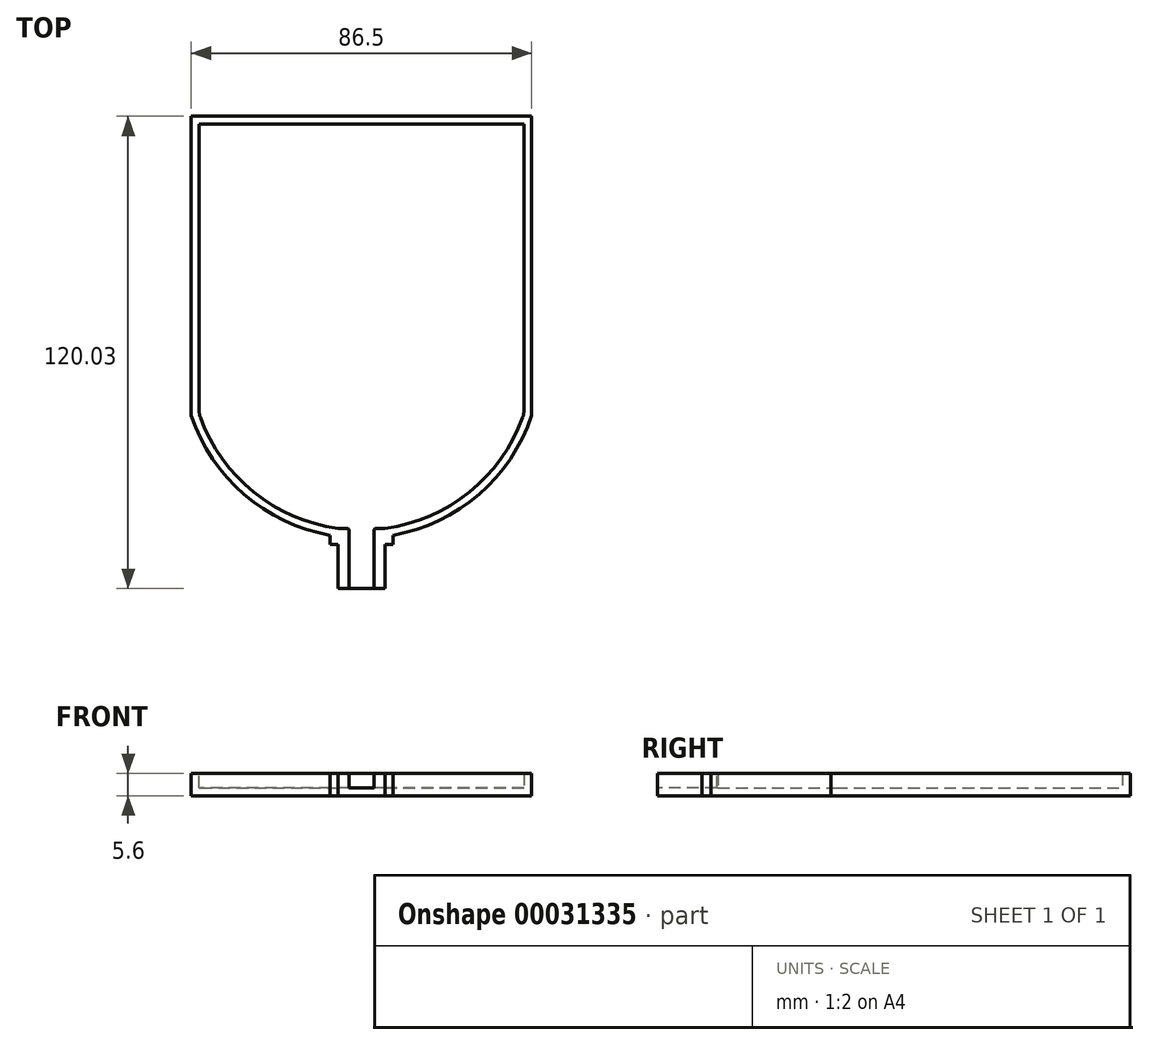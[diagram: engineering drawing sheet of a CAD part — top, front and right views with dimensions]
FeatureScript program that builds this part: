
annotation { "Feature Type Name" : "Feature", "Feature Type Description" : "" }
export const myFeature = defineFeature(function(context is Context, id is Id, definition is map)
    precondition{}
    {
        {
            var Q0;
            Q0=qCreatedBy(makeId("Top.planeOp"),FACE);
            var sketch = newSketch(context, id + "F0", { "sketchPlane" : qUnion([Q0])});
            skLineSegment(sketch, "E0.bottom", {"start": v(-41.08, 29.97) * mm, "end": v(45.42, 29.97) * mm});
            skLineSegment(sketch, "E0.top", {"start": v(-41.08, -46.03) * mm, "end": v(45.42, -46.03) * mm});
            skLineSegment(sketch, "E0.left", {"start": v(-41.08, 29.97) * mm, "end": v(-41.08, -46.03) * mm});
            skLineSegment(sketch, "E0.right", {"start": v(45.42, 29.97) * mm, "end": v(45.42, -46.03) * mm});
            skArc(sketch, "E1", {"start": v(-41.08, -46.03) * mm, "mid": v(2.17, -77.2) * mm, "end": v(45.42, -46.03) * mm});
            skLineSegment(sketch, "E2", {"start": v(2.17, -46.03) * mm, "end": v(2.17, -77.2) * mm});
            skLineSegment(sketch, "E3.bottom", {"start": v(2.17, -77.2) * mm, "end": v(8.1, -77.2) * mm});
            skLineSegment(sketch, "E3.top", {"start": v(2.17, -90.06) * mm, "end": v(8.1, -90.06) * mm});
            skLineSegment(sketch, "E3.left", {"start": v(2.17, -77.2) * mm, "end": v(2.17, -90.06) * mm});
            skLineSegment(sketch, "E3.right", {"start": v(8.1, -77.2) * mm, "end": v(8.1, -90.06) * mm});
            skLineSegment(sketch, "E4.bottom", {"start": v(2.17, -77.2) * mm, "end": v(-3.75, -77.2) * mm});
            skLineSegment(sketch, "E4.top", {"start": v(2.17, -90.06) * mm, "end": v(-3.75, -90.06) * mm});
            skLineSegment(sketch, "E4.right", {"start": v(-3.75, -77.2) * mm, "end": v(-3.75, -90.06) * mm});
            skLineSegment(sketch, "E5.bottom", {"start": v(-5.83, -76.5) * mm, "end": v(2.17, -76.5) * mm});
            skLineSegment(sketch, "E5.top", {"start": v(-5.83, -78.8) * mm, "end": v(2.17, -78.8) * mm});
            skLineSegment(sketch, "E5.left", {"start": v(-5.83, -76.5) * mm, "end": v(-5.83, -78.8) * mm});
            skLineSegment(sketch, "E5.right", {"start": v(2.17, -76.5) * mm, "end": v(2.17, -78.8) * mm});
            skLineSegment(sketch, "E6.bottom", {"start": v(2.17, -78.8) * mm, "end": v(10.17, -78.8) * mm});
            skLineSegment(sketch, "E6.top", {"start": v(2.17, -76.5) * mm, "end": v(10.17, -76.5) * mm});
            skLineSegment(sketch, "E6.left", {"start": v(2.17, -78.8) * mm, "end": v(2.17, -76.5) * mm});
            skLineSegment(sketch, "E6.right", {"start": v(10.17, -78.8) * mm, "end": v(10.17, -76.5) * mm});
            skLineSegment(sketch, "E7.0", {"start": v(-39.08, 27.97) * mm, "end": v(43.42, 27.97) * mm});
            skLineSegment(sketch, "E7.1", {"start": v(-39.08, 27.97) * mm, "end": v(-39.08, -45.7) * mm});
            skArc(sketch, "E7.2", {"start": v(-39.08, -45.7) * mm, "mid": v(2.17, -75.2) * mm, "end": v(43.42, -45.7) * mm});
            skLineSegment(sketch, "E7.3", {"start": v(43.42, 27.97) * mm, "end": v(43.42, -45.7) * mm});
            skSolve(sketch);
        }
        {
            var Q0;
            {var subQ1=sQuery(id+"F0.wireOp",EDGE,"E2");var subQ3=sQuery(id+"F0.wireOp",EDGE,"E0.top");var subQ5=makeQuery(id+"F0.imprint","INTERSECT",VERTEX,{"derivedFrom":[subQ3,subQ1]});Q0=makeQuery(id+"F0.imprint","IMPRINT",FACE,{"disambiguationData":[TD([[makeQuery(id+"F0.imprint","IMPRINT",EDGE,{"disambiguationData":[TD([[subQ5,-1.0]])],"derivedFrom":subQ3}),-1.0]])]});}
            var Q1;
            {var subQ1=sQuery(id+"F0.wireOp",EDGE,"E2");var subQ3=sQuery(id+"F0.wireOp",EDGE,"E0.top");var subQ5=makeQuery(id+"F0.imprint","INTERSECT",VERTEX,{"derivedFrom":[subQ3,subQ1]});Q1=makeQuery(id+"F0.imprint","IMPRINT",FACE,{"disambiguationData":[TD([[makeQuery(id+"F0.imprint","IMPRINT",EDGE,{"disambiguationData":[TD([[subQ5,1.0]])],"derivedFrom":subQ3}),-1.0]])]});}
            var Q2;
            Q2=makeQuery(id+"F0.imprint","IMPRINT",FACE,{"disambiguationData":[TD([[makeQuery(id+"F0.imprint","IMPRINT",EDGE,{"derivedFrom":sQuery(id+"F0.wireOp",EDGE,"E0.bottom")}),-1.0]])]});
            var Q3;
            {var subQ5=sQuery(id+"F0.wireOp",EDGE,"E5.bottom");Q3=makeQuery(id+"F0.imprint","IMPRINT",FACE,{"disambiguationData":[TD([[makeQuery(id+"F0.imprint","IMPRINT",EDGE,{"derivedFrom":subQ5}),1.0]])]});}
            var Q4;
            {var subQ5=sQuery(id+"F0.wireOp",EDGE,"E6.top");Q4=makeQuery(id+"F0.imprint","IMPRINT",FACE,{"disambiguationData":[TD([[makeQuery(id+"F0.imprint","IMPRINT",EDGE,{"derivedFrom":subQ5}),1.0]])]});}
            var Q5;
            Q5=makeQuery(id+"F0.imprint","IMPRINT",FACE,{"disambiguationData":[TD([[makeQuery(id+"F0.imprint","IMPRINT",EDGE,{"derivedFrom":sQuery(id+"F0.wireOp",EDGE,"E7.0")}),-1.0]])]});
            var Q6;
            {var subQ4=sQuery(id+"F0.wireOp",EDGE,"E3.top");Q6=makeQuery(id+"F0.imprint","IMPRINT",FACE,{"disambiguationData":[TD([[makeQuery(id+"F0.imprint","IMPRINT",EDGE,{"derivedFrom":subQ4}),1.0]])]});}
            var Q7;
            {var subQ4=sQuery(id+"F0.wireOp",EDGE,"E4.top");Q7=makeQuery(id+"F0.imprint","IMPRINT",FACE,{"disambiguationData":[TD([[makeQuery(id+"F0.imprint","IMPRINT",EDGE,{"derivedFrom":subQ4}),-1.0]])]});}
            var Q8;
            {var subQ3=sQuery(id+"F0.wireOp",EDGE,"E4.bottom");Q8=makeQuery(id+"F0.imprint","IMPRINT",FACE,{"disambiguationData":[TD([[makeQuery(id+"F0.imprint","IMPRINT",EDGE,{"derivedFrom":subQ3}),1.0]])]});}
            var Q9;
            {var subQ4=sQuery(id+"F0.wireOp",EDGE,"E4.bottom");Q9=makeQuery(id+"F0.imprint","IMPRINT",FACE,{"disambiguationData":[TD([[makeQuery(id+"F0.imprint","IMPRINT",EDGE,{"derivedFrom":subQ4}),-1.0]])]});}
            var Q10;
            {var subQ4=sQuery(id+"F0.wireOp",EDGE,"E3.bottom");Q10=makeQuery(id+"F0.imprint","IMPRINT",FACE,{"disambiguationData":[TD([[makeQuery(id+"F0.imprint","IMPRINT",EDGE,{"derivedFrom":subQ4}),1.0]])]});}
            var Q11;
            {var subQ3=sQuery(id+"F0.wireOp",EDGE,"E3.bottom");Q11=makeQuery(id+"F0.imprint","IMPRINT",FACE,{"disambiguationData":[TD([[makeQuery(id+"F0.imprint","IMPRINT",EDGE,{"derivedFrom":subQ3}),-1.0]])]});}
            var Q12;
            {var subQ3=sQuery(id+"F0.wireOp",EDGE,"E5.bottom");Q12=makeQuery(id+"F0.imprint","IMPRINT",FACE,{"disambiguationData":[TD([[makeQuery(id+"F0.imprint","IMPRINT",EDGE,{"derivedFrom":subQ3}),-1.0]])]});}
            var Q13;
            {var subQ3=sQuery(id+"F0.wireOp",EDGE,"E6.top");Q13=makeQuery(id+"F0.imprint","IMPRINT",FACE,{"disambiguationData":[TD([[makeQuery(id+"F0.imprint","IMPRINT",EDGE,{"derivedFrom":subQ3}),-1.0]])]});}
            var Q14;
            Q14=sQuery(id+"F0.wireOp",EDGE,"E0.bottom");
            var Q15;
            Q15=sQuery(id+"F0.wireOp",EDGE,"E0.right");
            var Q16;
            Q16=sQuery(id+"F0.wireOp",EDGE,"E1");
            var Q17;
            Q17=sQuery(id+"F0.wireOp",EDGE,"E0.left");
            extrude(context, id + "F1", {"entities" : qUnion([Q0, Q1, Q2, Q3, Q4, Q5, Q6, Q7, Q8, Q9, Q10, Q11, Q12, Q13]), "surfaceEntities" : qUnion([Q14, Q15, Q16, Q17]), "endBound" : BoundingType.SYMMETRIC, "depth" : 2 * mm});
        }
        {
            var Q0;
            Q0=makeQuery(id+"F1.opExtrude","CAP_FACE",FACE,{"disambiguationData":[OSD([sQuery(id+"F0.wireOp",EDGE,"E0.bottom"),sQuery(id+"F0.wireOp",EDGE,"E0.left"),sQuery(id+"F0.wireOp",EDGE,"E0.right"),sQuery(id+"F0.wireOp",EDGE,"E1"),sQuery(id+"F0.wireOp",EDGE,"E3.top"),sQuery(id+"F0.wireOp",EDGE,"E3.right"),sQuery(id+"F0.wireOp",EDGE,"E4.top"),sQuery(id+"F0.wireOp",EDGE,"E4.right"),sQuery(id+"F0.wireOp",EDGE,"E5.top"),sQuery(id+"F0.wireOp",EDGE,"E5.left"),sQuery(id+"F0.wireOp",EDGE,"E6.bottom"),sQuery(id+"F0.wireOp",EDGE,"E6.right")])],"isStart":false});
            var sketch = newSketch(context, id + "F2", { "sketchPlane" : qUnion([Q0])});
            skLineSegment(sketch, "E8.0", {"start": v(43.42, 27.97) * mm, "end": v(-39.08, 27.97) * mm});
            skLineSegment(sketch, "E8.1", {"start": v(43.42, -45.7) * mm, "end": v(43.42, 27.97) * mm});
            skArc(sketch, "E8.2", {"start": v(8.17, -74.8) * mm, "mid": v(29.92, -65.24) * mm, "end": v(43.42, -45.7) * mm});
            skLineSegment(sketch, "E8.3", {"start": v(8.17, -76.8) * mm, "end": v(8.17, -74.8) * mm});
            skLineSegment(sketch, "E8.4", {"start": v(6.1, -76.8) * mm, "end": v(8.17, -76.8) * mm});
            skLineSegment(sketch, "E8.5", {"start": v(-39.08, 27.97) * mm, "end": v(-39.08, -45.7) * mm});
            skLineSegment(sketch, "E8.6", {"start": v(6.1, -88.06) * mm, "end": v(6.1, -76.8) * mm});
            skLineSegment(sketch, "E8.7", {"start": v(-1.75, -88.06) * mm, "end": v(6.1, -88.06) * mm});
            skLineSegment(sketch, "E8.8", {"start": v(-1.75, -76.8) * mm, "end": v(-1.75, -88.06) * mm});
            skLineSegment(sketch, "E8.9", {"start": v(-3.83, -76.8) * mm, "end": v(-1.75, -76.8) * mm});
            skLineSegment(sketch, "E8.10", {"start": v(-3.83, -74.8) * mm, "end": v(-3.83, -76.8) * mm});
            skArc(sketch, "E8.11", {"start": v(-39.08, -45.7) * mm, "mid": v(-25.57, -65.24) * mm, "end": v(-3.83, -74.8) * mm});
            skLineSegment(sketch, "E9", {"start": v(2.17, -88.06) * mm, "end": v(2.17, -74.8) * mm});
            skLineSegment(sketch, "E10", {"start": v(2.17, -74.8) * mm, "end": v(5.32, -74.8) * mm});
            skLineSegment(sketch, "E11", {"start": v(5.32, -74.8) * mm, "end": v(2.17, -74.8) * mm});
            skLineSegment(sketch, "E12", {"start": v(2.17, -74.8) * mm, "end": v(-0.98, -74.8) * mm});
            skLineSegment(sketch, "E13", {"start": v(-0.98, -74.8) * mm, "end": v(-0.98, -90.06) * mm});
            skLineSegment(sketch, "E14", {"start": v(-0.98, -90.06) * mm, "end": v(5.32, -90.06) * mm});
            skLineSegment(sketch, "E15", {"start": v(5.32, -90.06) * mm, "end": v(5.32, -74.8) * mm});
            skLineSegment(sketch, "E16", {"start": v(8.17, -74.8) * mm, "end": v(5.32, -74.8) * mm});
            skLineSegment(sketch, "E17", {"start": v(-0.98, -74.8) * mm, "end": v(-3.83, -74.8) * mm});
            skSolve(sketch);
        }
        {
            var Q0;
            Q0=makeQuery(id+"F2.imprint","IMPRINT",FACE,{"disambiguationData":[TD([[makeQuery(id+"F2.imprint","IMPRINT",EDGE,{"derivedFrom":sQuery(id+"F2.wireOp",EDGE,"E8.0")}),-1.0]])]});
            var Q1;
            {var subQ4=sQuery(id+"F2.wireOp",EDGE,"E8.8");Q1=makeQuery(id+"F2.imprint","IMPRINT",FACE,{"disambiguationData":[TD([[makeQuery(id+"F2.imprint","IMPRINT",EDGE,{"derivedFrom":subQ4}),1.0]])]});}
            var Q2;
            Q2=makeQuery(id+"F2.imprint","IMPRINT",FACE,{"disambiguationData":[TD([[makeQuery(id+"F2.imprint","IMPRINT",EDGE,{"derivedFrom":sQuery(id+"F2.wireOp",EDGE,"E8.3")}),1.0]])]});
            extrude(context, id + "F3", {"entities" : qUnion([Q0, Q1, Q2]), "operationType" : NewBodyOperationType.ADD, "depth" : 3.6 * mm});
        }
        {
            var Q0;
            Q0=makeQuery(id+"F3.opExtrude","SWEPT_EDGE",EDGE,{"disambiguationData":[OSD([sQuery(id+"F2.wireOp",EDGE,"E8.5"),sQuery(id+"F2.wireOp",EDGE,"E8.11")])]});
            var Q1;
            Q1=makeQuery(id+"F3.opExtrude","SWEPT_EDGE",EDGE,{"disambiguationData":[OSD([sQuery(id+"F2.wireOp",EDGE,"E8.1"),sQuery(id+"F2.wireOp",EDGE,"E8.2")])]});
            fillet(context, id + "F4", {"entities" : qUnion([Q0, Q1]), "radius" : 5 * mm, "tangentPropagation" : true, "allowEdgeOverflow" : false});
        }
        {
            var Q0;
            Q0=makeQuery(id+"F3.opExtrude","SWEPT_EDGE",EDGE,{"disambiguationData":[OSD([sQuery(id+"F2.wireOp",EDGE,"E12"),sQuery(id+"F2.wireOp",EDGE,"E13"),sQuery(id+"F2.wireOp",EDGE,"E17")])]});
            var Q1;
            Q1=makeQuery(id+"F3.opExtrude","SWEPT_EDGE",EDGE,{"disambiguationData":[OSD([sQuery(id+"F2.wireOp",EDGE,"E11"),sQuery(id+"F2.wireOp",EDGE,"E15"),sQuery(id+"F2.wireOp",EDGE,"E16")])]});
            chamfer(context, id + "F5", {"entities" : qUnion([Q0, Q1]), "width" : .25 * mm, "tangentPropagation" : true});
        }
    });
